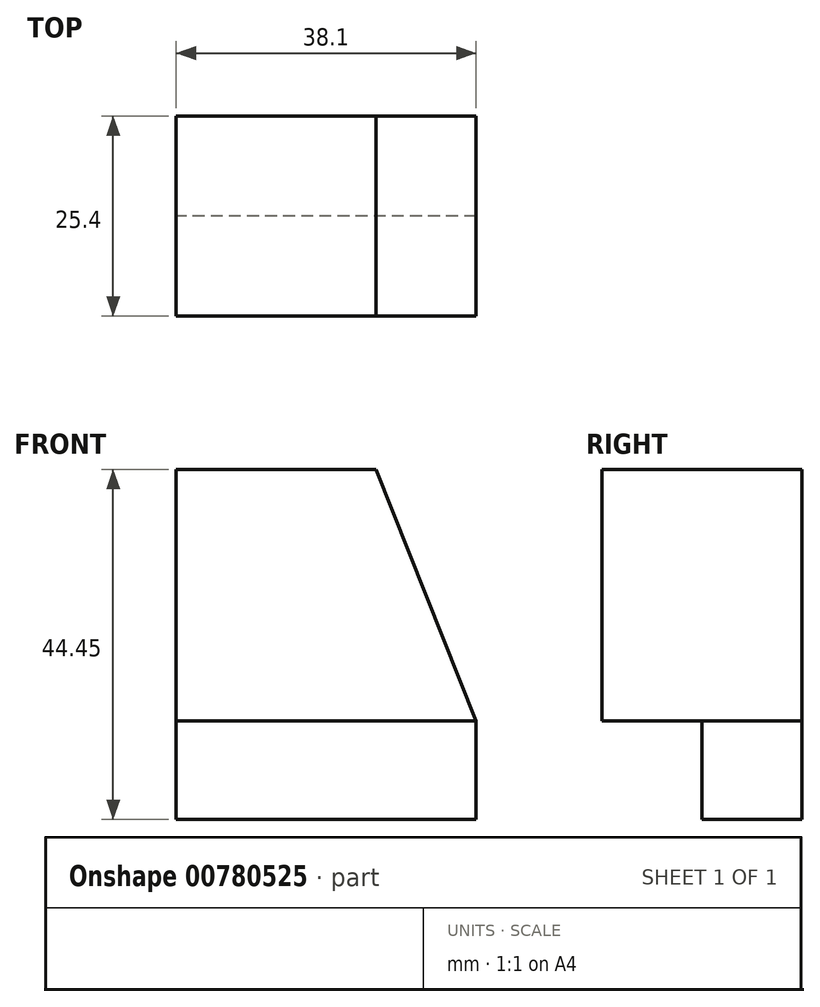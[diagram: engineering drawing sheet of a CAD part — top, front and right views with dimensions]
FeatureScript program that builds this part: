
annotation { "Feature Type Name" : "Feature", "Feature Type Description" : "" }
export const myFeature = defineFeature(function(context is Context, id is Id, definition is map)
    precondition{}
    {
        {
            var Q0;
            Q0=qCreatedBy(makeId("Front.planeOp"),FACE);
            var sketch = newSketch(context, id + "F0", { "sketchPlane" : qUnion([Q0])});
            skLineSegment(sketch, "E0", {"start": v(0, 0) * mm, "end": v(38.1, 0) * mm});
            skLineSegment(sketch, "E1", {"start": v(38.1, 0) * mm, "end": v(38.1, 44.45) * mm});
            skLineSegment(sketch, "E2", {"start": v(38.1, 44.45) * mm, "end": v(0, 44.45) * mm});
            skLineSegment(sketch, "E3", {"start": v(0, 44.45) * mm, "end": v(0, 0) * mm});
            skSolve(sketch);
        }
        {
            var Q0;
            Q0=makeQuery(id+"F0.imprint","IMPRINT",FACE,{"disambiguationData":[TD([[makeQuery(id+"F0.imprint","IMPRINT",EDGE,{"derivedFrom":sQuery(id+"F0.wireOp",EDGE,"E0")}),1.0]])]});
            extrude(context, id + "F1", {"entities" : qUnion([Q0]), "depth" : 12.7 * mm, "offsetDistance" : 25.4 * mm});
        }
        {
            var Q0;
            Q0=makeQuery(id+"F1.opExtrude","CAP_FACE",FACE,{"disambiguationData":[OSD([sQuery(id+"F0.wireOp",EDGE,"E0"),sQuery(id+"F0.wireOp",EDGE,"E1"),sQuery(id+"F0.wireOp",EDGE,"E2"),sQuery(id+"F0.wireOp",EDGE,"E3")])],"isStart":false});
            var sketch = newSketch(context, id + "F2", { "sketchPlane" : qUnion([Q0])});
            skLineSegment(sketch, "E4", {"start": v(0, 44.45) * mm, "end": v(25.4, 44.45) * mm});
            skLineSegment(sketch, "E5", {"start": v(25.4, 44.45) * mm, "end": v(38.1, 12.5) * mm});
            skSolve(sketch);
        }
        {
            var Q0;
            {var subQ0=sQuery(id+"F2.wireOp",EDGE,"E5");Q0=makeQuery(id+"F2.imprint","IMPRINT",FACE,{"disambiguationData":[TD([[makeQuery(id+"F2.imprint","IMPRINT",EDGE,{"derivedFrom":subQ0}),1.0]])]});}
            extrude(context, id + "F3", {"entities" : qUnion([Q0]), "operationType" : NewBodyOperationType.REMOVE, "oppositeDirection" : true, "depth" : 25.4 * mm, "offsetDistance" : 25.4 * mm});
        }
        {
            var Q0;
            Q0=makeQuery(id+"F1.opExtrude","CAP_FACE",FACE,{"disambiguationData":[OSD([sQuery(id+"F0.wireOp",EDGE,"E0"),sQuery(id+"F0.wireOp",EDGE,"E1"),sQuery(id+"F0.wireOp",EDGE,"E2"),sQuery(id+"F0.wireOp",EDGE,"E3")])],"isStart":false});
            var sketch = newSketch(context, id + "F4", { "sketchPlane" : qUnion([Q0])});
            skLineSegment(sketch, "E6", {"start": v(38.1, 12.5) * mm, "end": v(0, 12.5) * mm});
            skSolve(sketch);
        }
        {
            var Q0;
            {var subQ0=sQuery(id+"F4.wireOp",EDGE,"E6");Q0=makeQuery(id+"F4.imprint","IMPRINT",FACE,{"disambiguationData":[TD([[makeQuery(id+"F4.imprint","IMPRINT",EDGE,{"derivedFrom":subQ0}),-1.0]])]});}
            extrude(context, id + "F5", {"entities" : qUnion([Q0]), "operationType" : NewBodyOperationType.ADD, "surfaceOperationType" : NewSurfaceOperationType.ADD, "depth" : 12.7 * mm, "offsetDistance" : 25.4 * mm});
        }
    });
